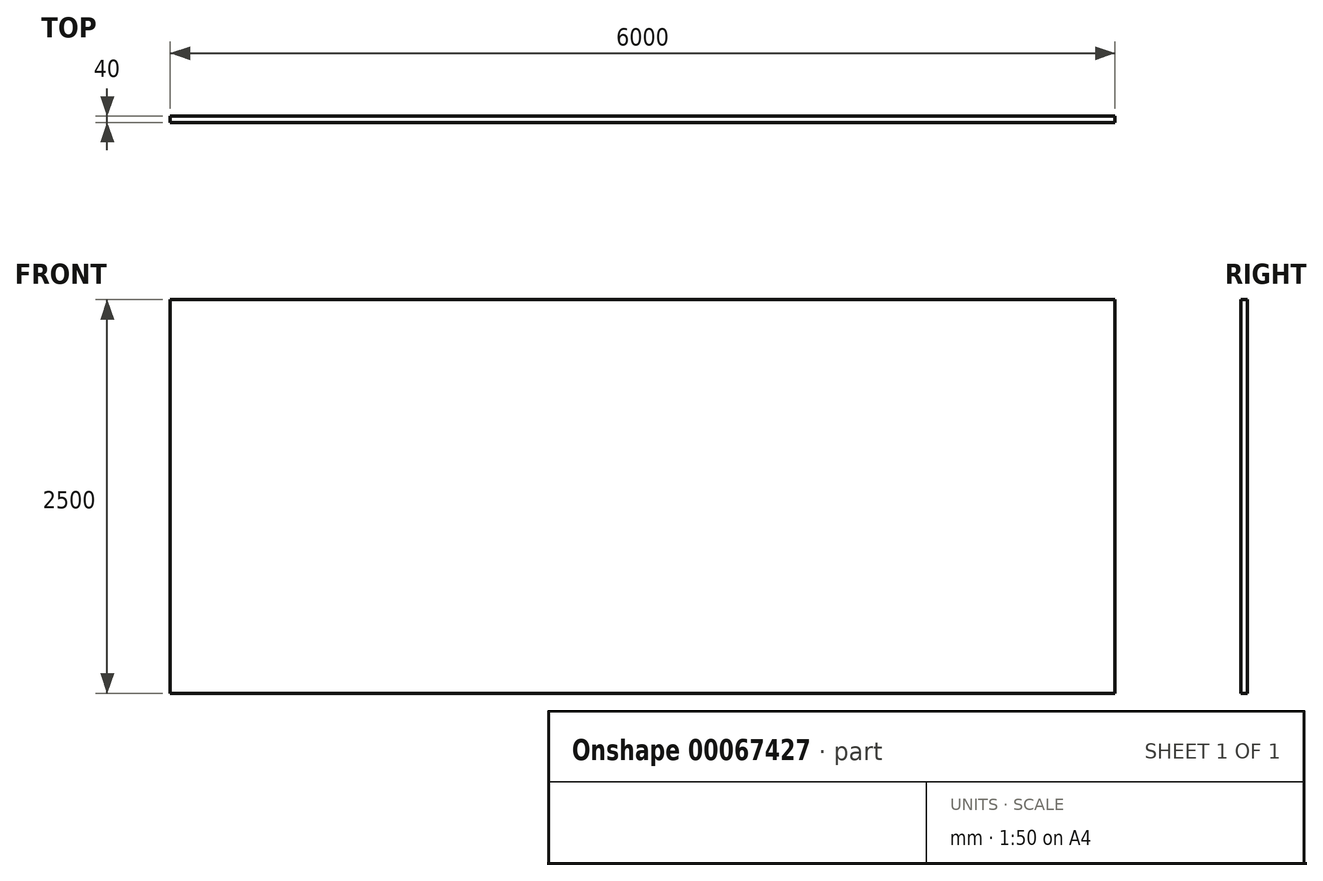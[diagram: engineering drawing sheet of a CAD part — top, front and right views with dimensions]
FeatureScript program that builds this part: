
annotation { "Feature Type Name" : "Feature", "Feature Type Description" : "" }
export const myFeature = defineFeature(function(context is Context, id is Id, definition is map)
    precondition{}
    {
        {
            var Q0;
            Q0=qCreatedBy(makeId("Front.planeOp"),FACE);
            var sketch = newSketch(context, id + "F0", { "sketchPlane" : qUnion([Q0])});
            skLineSegment(sketch, "E0.bottom", {"start": v(-126.4, 2339.64) * mm, "end": v(5873.6, 2339.64) * mm});
            skLineSegment(sketch, "E0.top", {"start": v(-126.4, -160.36) * mm, "end": v(5873.6, -160.36) * mm});
            skLineSegment(sketch, "E0.left", {"start": v(-126.4, 2339.64) * mm, "end": v(-126.4, -160.36) * mm});
            skLineSegment(sketch, "E0.right", {"start": v(5873.6, 2339.64) * mm, "end": v(5873.6, -160.36) * mm});
            skSolve(sketch);
        }
        {
            var Q0;
            Q0 = qSketchRegion(id + "F0", true);
            extrude(context, id + "F1", {"entities" : qUnion([Q0]), "depth" : 40 * mm});
        }
    });
